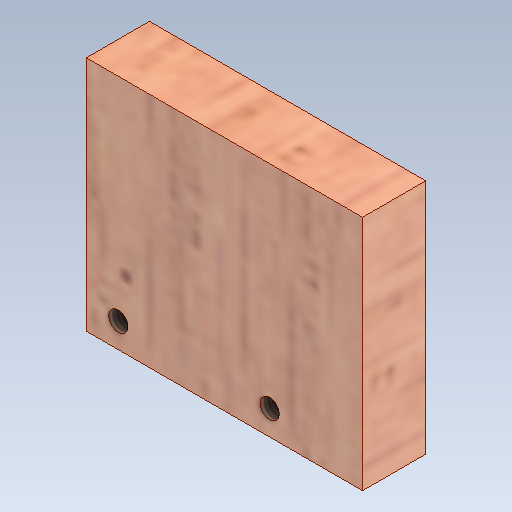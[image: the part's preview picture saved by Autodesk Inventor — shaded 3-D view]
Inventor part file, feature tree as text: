
AUTODESK INVENTOR PART (.ipt)
format: ipt  version: 2020 (Build 240168000, 168)  size: 226,816 bytes
history: native  units: mm
features: other x3, sketch x2, reference x2, extrude x1, hole x1
ambient origin geometry x8: Origin, YZ Plane, XZ Plane, XY Plane, X Axis, Y Axis, Z Axis, Center Point
bodies: Solid1 (feature_tree)
feature tree (9):
  extrude  "Extrusion1"  Depth=30.0mm
  hole  "Hole1"  [1 undecoded]
  sketch  "Sketch1"  dims[d0=35.0mm d1=30.0mm]
  sketch  "Sketch6"  dims[d2=8.0mm d3=0.0mm d37=2.459mm d38=8.0mm d39=4.0mm d40=2.0mm d41=90.0deg d42=8.8mm d43=20.594885mm]
  reference  "Reference1"
  reference  "Reference2"
  parser-record x1  (decoder bookkeeping rows leaked as tree rows — omitted from the tree; the rows remain in map.json)
  other  "0005-00-00 Ansamblu_General_V1.iam"
  other  "0005-20-1003 Switch:1"
note: 1 required parameter value undecoded (feature->parameter linkage not recoverable at this tier; creation-order binding heuristic only, values carry confidence <= 0.55)
note: 1 file-system path scrubbed to <path> (originals preserved in map.json)
